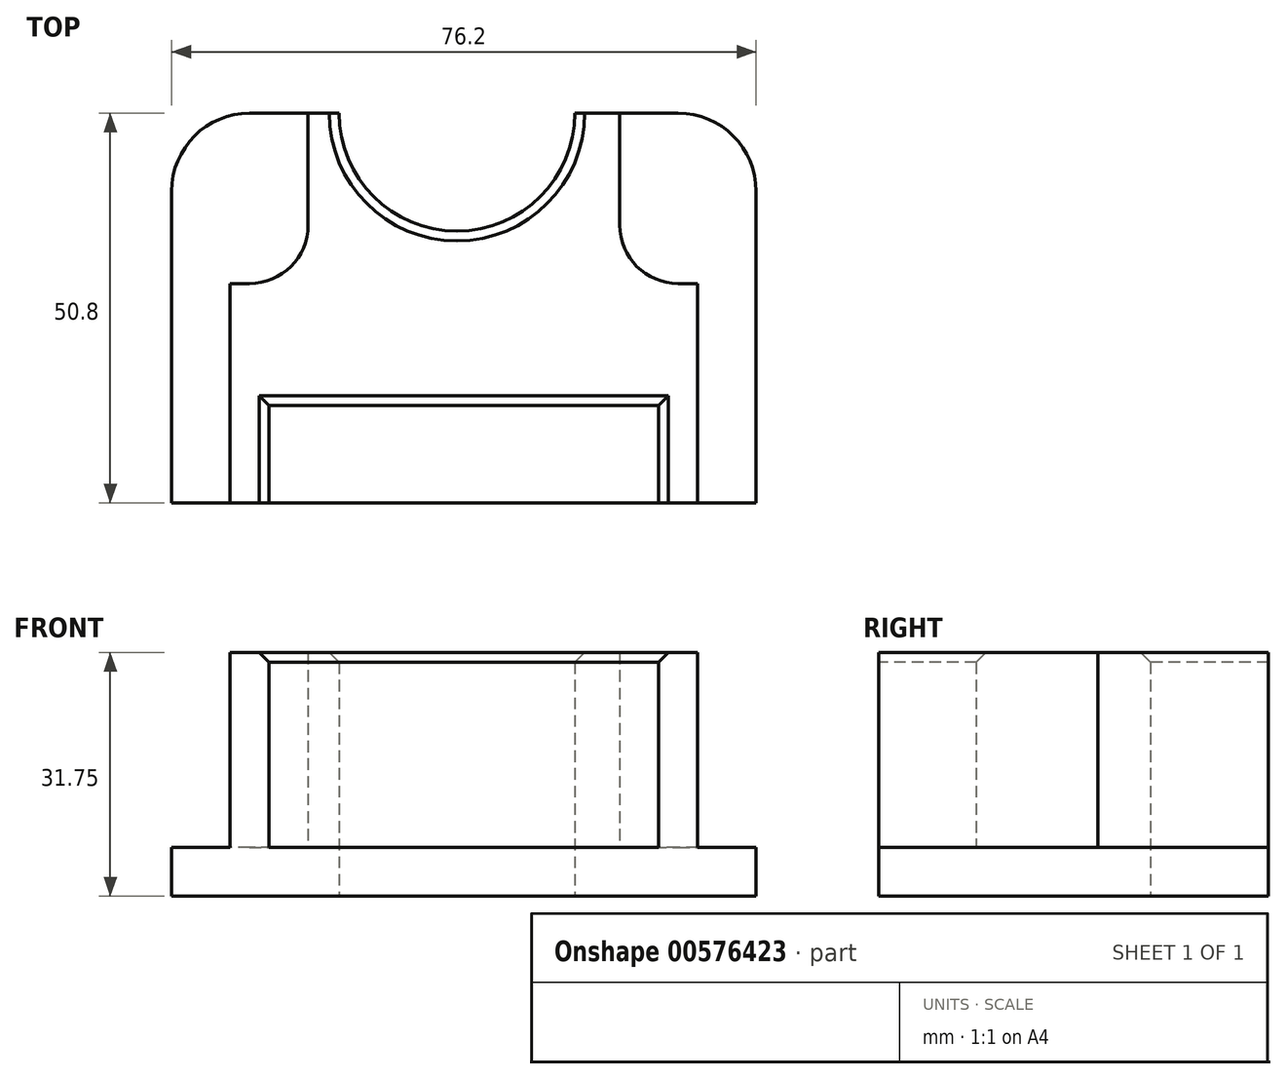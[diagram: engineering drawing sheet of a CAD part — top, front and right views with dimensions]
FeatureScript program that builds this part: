
annotation { "Feature Type Name" : "Feature", "Feature Type Description" : "" }
export const myFeature = defineFeature(function(context is Context, id is Id, definition is map)
    precondition{}
    {
        {
            var Q0;
            Q0=qCreatedBy(makeId("Top.planeOp"),FACE);
            var sketch = newSketch(context, id + "F0", { "sketchPlane" : qUnion([Q0])});
            skLineSegment(sketch, "E0.bottom", {"start": v(38.1, 25.4) * mm, "end": v(-38.1, 25.4) * mm});
            skLineSegment(sketch, "E0.top", {"start": v(38.1, -25.4) * mm, "end": v(-38.1, -25.4) * mm});
            skLineSegment(sketch, "E0.left", {"start": v(38.1, 25.4) * mm, "end": v(38.1, -25.4) * mm});
            skLineSegment(sketch, "E0.right", {"start": v(-38.1, 25.4) * mm, "end": v(-38.1, -25.4) * mm});
            skPoint(sketch, "E0.middle", {"position": v(0, 0) * mm});
            skSolve(sketch);
        }
        {
            var Q0;
            Q0 = qSketchRegion(id + "F0", true);
            extrude(context, id + "F1", {"entities" : qUnion([Q0]), "depth" : 6.35 * mm, "offsetDistance" : 25.4 * mm});
        }
        {
            var Q0;
            Q0=makeQuery(id+"F1.opExtrude","CAP_FACE",FACE,{"disambiguationData":[OSD([sQuery(id+"F0.wireOp",EDGE,"E0.bottom"),sQuery(id+"F0.wireOp",EDGE,"E0.top"),sQuery(id+"F0.wireOp",EDGE,"E0.left"),sQuery(id+"F0.wireOp",EDGE,"E0.right")])],"isStart":false});
            var sketch = newSketch(context, id + "F2", { "sketchPlane" : qUnion([Q0])});
            skLineSegment(sketch, "E1.bottom", {"start": v(25.4, 25.4) * mm, "end": v(-25.4, 25.4) * mm});
            skLineSegment(sketch, "E1.top", {"start": v(25.4, -12.7) * mm, "end": v(-25.4, -12.7) * mm});
            skLineSegment(sketch, "E1.left", {"start": v(25.4, 25.4) * mm, "end": v(25.4, -12.7) * mm});
            skLineSegment(sketch, "E1.right", {"start": v(-25.4, 25.4) * mm, "end": v(-25.4, -12.7) * mm});
            skLineSegment(sketch, "E2.bottom", {"start": v(-25.4, 25.4) * mm, "end": v(-20.32, 25.4) * mm});
            skLineSegment(sketch, "E2.top", {"start": v(-25.4, 3.18) * mm, "end": v(-20.32, 3.18) * mm});
            skLineSegment(sketch, "E2.left", {"start": v(-25.4, 25.4) * mm, "end": v(-25.4, 3.18) * mm});
            skLineSegment(sketch, "E2.right", {"start": v(-20.32, 25.4) * mm, "end": v(-20.32, 3.18) * mm});
            skLineSegment(sketch, "E3.bottom", {"start": v(25.4, 25.4) * mm, "end": v(20.32, 25.4) * mm});
            skLineSegment(sketch, "E3.top", {"start": v(25.4, 3.18) * mm, "end": v(20.32, 3.18) * mm});
            skLineSegment(sketch, "E3.left", {"start": v(25.4, 25.4) * mm, "end": v(25.4, 3.18) * mm});
            skLineSegment(sketch, "E3.right", {"start": v(20.32, 25.4) * mm, "end": v(20.32, 3.18) * mm});
            skLineSegment(sketch, "E4.bottom", {"start": v(-25.4, 3.18) * mm, "end": v(-30.48, 3.18) * mm});
            skLineSegment(sketch, "E4.top", {"start": v(-25.4, -25.4) * mm, "end": v(-30.48, -25.4) * mm});
            skLineSegment(sketch, "E4.left", {"start": v(-25.4, 3.18) * mm, "end": v(-25.4, -25.4) * mm});
            skLineSegment(sketch, "E4.right", {"start": v(-30.48, 3.18) * mm, "end": v(-30.48, -25.4) * mm});
            skLineSegment(sketch, "E5.bottom", {"start": v(25.4, 3.18) * mm, "end": v(30.48, 3.18) * mm});
            skLineSegment(sketch, "E5.top", {"start": v(25.4, -25.4) * mm, "end": v(30.48, -25.4) * mm});
            skLineSegment(sketch, "E5.left", {"start": v(25.4, 3.18) * mm, "end": v(25.4, -25.4) * mm});
            skLineSegment(sketch, "E5.right", {"start": v(30.48, 3.18) * mm, "end": v(30.48, -25.4) * mm});
            skArc(sketch, "E6", {"start": v(-16.28, 25.4) * mm, "mid": v(-0.9, 10.02) * mm, "end": v(14.48, 25.4) * mm});
            skSolve(sketch);
        }
        {
            var Q0;
            {var subQ3=sQuery(id+"F2.wireOp",EDGE,"E4.bottom");Q0=makeQuery(id+"F2.imprint","IMPRINT",FACE,{"disambiguationData":[TD([[makeQuery(id+"F2.imprint","IMPRINT",EDGE,{"derivedFrom":subQ3}),1.0]])]});}
            var Q1;
            {var subQ3=sQuery(id+"F2.wireOp",EDGE,"E5.bottom");Q1=makeQuery(id+"F2.imprint","IMPRINT",FACE,{"disambiguationData":[TD([[makeQuery(id+"F2.imprint","IMPRINT",EDGE,{"derivedFrom":subQ3}),-1.0]])]});}
            var Q2;
            {var subQ0=sQuery(id+"F2.wireOp",EDGE,"E1.top");Q2=makeQuery(id+"F2.imprint","IMPRINT",FACE,{"disambiguationData":[TD([[makeQuery(id+"F2.imprint","IMPRINT",EDGE,{"derivedFrom":subQ0}),-1.0]])]});}
            extrude(context, id + "F3", {"entities" : qUnion([Q0, Q1, Q2]), "operationType" : NewBodyOperationType.ADD, "depth" : 25.4 * mm, "offsetDistance" : 25.4 * mm});
        }
        {
            var Q0;
            Q0=makeQuery(id+"F3.opExtrude","CAP_FACE",FACE,{"disambiguationData":[OSD([sQuery(id+"F2.wireOp",EDGE,"E1.bottom"),sQuery(id+"F2.wireOp",EDGE,"E1.top"),sQuery(id+"F2.wireOp",EDGE,"E2.top"),sQuery(id+"F2.wireOp",EDGE,"E2.right"),sQuery(id+"F2.wireOp",EDGE,"E3.top"),sQuery(id+"F2.wireOp",EDGE,"E3.right"),sQuery(id+"F2.wireOp",EDGE,"E4.bottom"),sQuery(id+"F2.wireOp",EDGE,"E4.top"),sQuery(id+"F2.wireOp",EDGE,"E4.left"),sQuery(id+"F2.wireOp",EDGE,"E4.right"),sQuery(id+"F2.wireOp",EDGE,"E5.bottom"),sQuery(id+"F2.wireOp",EDGE,"E5.top"),sQuery(id+"F2.wireOp",EDGE,"E5.left"),sQuery(id+"F2.wireOp",EDGE,"E5.right"),sQuery(id+"F2.wireOp",EDGE,"E6")])],"isStart":false});
            var sketch = newSketch(context, id + "F4", { "sketchPlane" : qUnion([Q0])});
            skArc(sketch, "E7", {"start": v(-16.28, 25.4) * mm, "mid": v(-0.9, 10.02) * mm, "end": v(14.48, 25.4) * mm});
            skLineSegment(sketch, "E8", {"start": v(-16.28, 25.4) * mm, "end": v(14.48, 25.4) * mm});
            skSolve(sketch);
        }
        {
            var Q0;
            Q0=makeQuery(id+"F4.imprint","IMPRINT",FACE,{"disambiguationData":[TD([[makeQuery(id+"F4.imprint","IMPRINT",EDGE,{"derivedFrom":sQuery(id+"F4.wireOp",EDGE,"E7")}),1.0]])]});
            extrude(context, id + "F5", {"entities" : qUnion([Q0]), "operationType" : NewBodyOperationType.REMOVE, "oppositeDirection" : true, "depth" : 31.75 * mm, "offsetDistance" : 25.4 * mm});
        }
        {
            var Q0;
            Q0=makeQuery(id+"F3.opExtrude","CAP_EDGE",EDGE,{"disambiguationData":[OSD([sQuery(id+"F2.wireOp",EDGE,"E1.top")])],"isStart":false});
            var Q1;
            Q1=makeQuery(id+"F3.opExtrude","CAP_EDGE",EDGE,{"disambiguationData":[OSD([sQuery(id+"F2.wireOp",EDGE,"E4.left")])],"isStart":false});
            var Q2;
            Q2=makeQuery(id+"F3.opExtrude","CAP_EDGE",EDGE,{"disambiguationData":[OSD([sQuery(id+"F2.wireOp",EDGE,"E5.left")])],"isStart":false});
            chamfer(context, id + "F6", {"entities" : qUnion([Q0, Q1, Q2]), "width" : 1.27 * mm, "tangentPropagation" : true});
        }
        {
            var Q0;
            Q0=makeQuery(id+"F1.opExtrude","SWEPT_EDGE",EDGE,{"disambiguationData":[OSD([sQuery(id+"F0.wireOp",EDGE,"E0.bottom"),sQuery(id+"F0.wireOp",EDGE,"E0.right")])]});
            var Q1;
            Q1=makeQuery(id+"F1.opExtrude","SWEPT_EDGE",EDGE,{"disambiguationData":[OSD([sQuery(id+"F0.wireOp",EDGE,"E0.bottom"),sQuery(id+"F0.wireOp",EDGE,"E0.left")])]});
            fillet(context, id + "F7", {"entities" : qUnion([Q0, Q1]), "radius" : 10.16 * mm, "tangentPropagation" : true, "allowEdgeOverflow" : false});
        }
        {
            var Q0;
            Q0=makeQuery(id+"F3.opExtrude","CAP_EDGE",EDGE,{"disambiguationData":[OSD([sQuery(id+"F2.wireOp",EDGE,"E6")])],"isStart":false});
            chamfer(context, id + "F8", {"entities" : qUnion([Q0]), "width" : 1.27 * mm, "tangentPropagation" : true});
        }
        {
            var Q0;
            Q0=makeQuery(id+"F3.opExtrude","SWEPT_EDGE",EDGE,{"disambiguationData":[OSD([sQuery(id+"F2.wireOp",EDGE,"E2.top"),sQuery(id+"F2.wireOp",EDGE,"E2.right")])]});
            fillet(context, id + "F9", {"entities" : qUnion([Q0]), "radius" : 7.62 * mm, "tangentPropagation" : true, "allowEdgeOverflow" : false});
        }
        {
            var Q0;
            Q0=makeQuery(id+"F3.opExtrude","SWEPT_EDGE",EDGE,{"disambiguationData":[OSD([sQuery(id+"F2.wireOp",EDGE,"E3.top"),sQuery(id+"F2.wireOp",EDGE,"E3.right")])]});
            fillet(context, id + "F10", {"entities" : qUnion([Q0]), "radius" : 7.62 * mm, "tangentPropagation" : true, "allowEdgeOverflow" : false});
        }
    });
